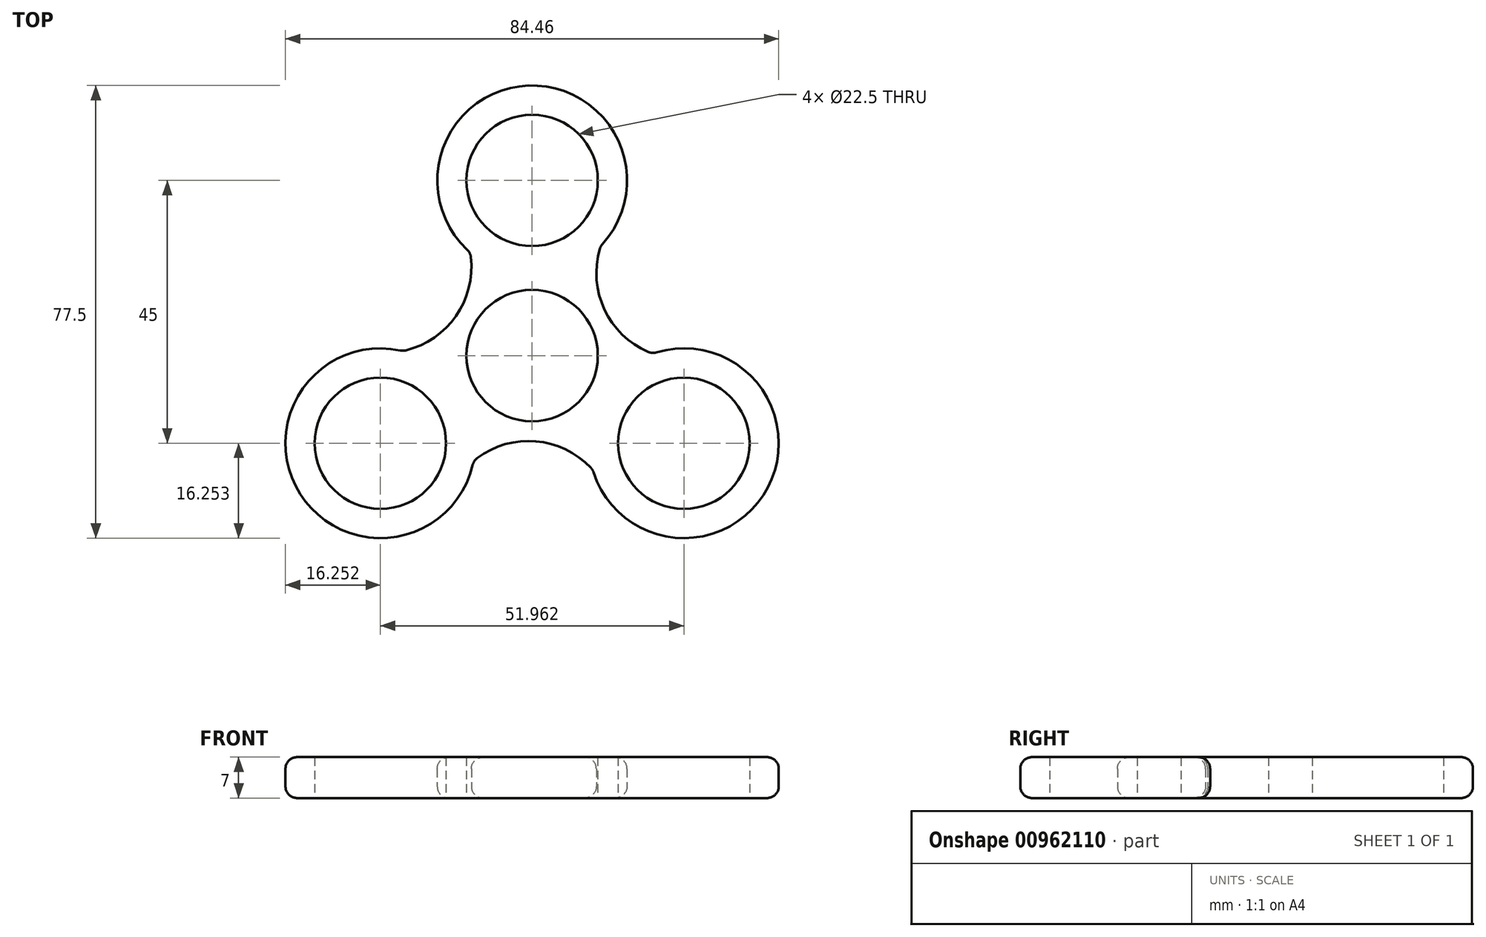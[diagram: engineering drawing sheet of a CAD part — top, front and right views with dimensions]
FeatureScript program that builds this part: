
annotation { "Feature Type Name" : "Feature", "Feature Type Description" : "" }
export const myFeature = defineFeature(function(context is Context, id is Id, definition is map)
    precondition{}
    {
        {
            var Q0;
            Q0=qCreatedBy(makeId("Top.planeOp"),FACE);
            var sketch = newSketch(context, id + "F0", { "sketchPlane" : qUnion([Q0])});
            skCircle(sketch, "E0", {"center": v(-12.85, 13.48) * mm, "radius": 11.25 * mm});
            skCircle(sketch, "E1", {"center": v(-12.85, 43.48) * mm, "radius": 11.25 * mm});
            skCircle(sketch, "E2.1.0", {"center": v(-38.83, -1.52) * mm, "radius": 11.25 * mm});
            skCircle(sketch, "E2.2.0", {"center": v(13.13, -1.52) * mm, "radius": 11.25 * mm});
            skCircle(sketch, "E3.0", {"center": v(-12.85, 43.48) * mm, "radius": 16.25 * mm});
            skCircle(sketch, "E4.0", {"center": v(13.13, -1.52) * mm, "radius": 16.25 * mm});
            skCircle(sketch, "E5.0", {"center": v(-38.83, -1.52) * mm, "radius": 16.25 * mm});
            skArc(sketch, "E6", {"start": v(-34.98, 14.27) * mm, "mid": v(-25.8, 20.39) * mm, "end": v(-23.46, 31.18) * mm});
            skArc(sketch, "E7.1.0", {"start": v(-2.46, -6.08) * mm, "mid": v(-12.35, -1.18) * mm, "end": v(-22.86, -4.55) * mm});
            skArc(sketch, "E7.2.0", {"start": v(-1.1, 32.26) * mm, "mid": v(-0.4, 21.24) * mm, "end": v(7.78, 13.83) * mm});
            skSolve(sketch);
        }
        {
            var Q0;
            Q0=makeQuery(id+"F0.imprint","IMPRINT",FACE,{"disambiguationData":[TD([[makeQuery(id+"F0.imprint","IMPRINT",EDGE,{"derivedFrom":sQuery(id+"F0.wireOp",EDGE,"E1")}),-1.0]])]});
            var Q1;
            Q1=makeQuery(id+"F0.imprint","IMPRINT",FACE,{"disambiguationData":[TD([[makeQuery(id+"F0.imprint","IMPRINT",EDGE,{"derivedFrom":sQuery(id+"F0.wireOp",EDGE,"E0")}),-1.0]])]});
            var Q2;
            Q2=makeQuery(id+"F0.imprint","IMPRINT",FACE,{"disambiguationData":[TD([[makeQuery(id+"F0.imprint","IMPRINT",EDGE,{"derivedFrom":sQuery(id+"F0.wireOp",EDGE,"E2.1.0")}),-1.0]])]});
            var Q3;
            Q3=makeQuery(id+"F0.imprint","IMPRINT",FACE,{"disambiguationData":[TD([[makeQuery(id+"F0.imprint","IMPRINT",EDGE,{"derivedFrom":sQuery(id+"F0.wireOp",EDGE,"E2.2.0")}),-1.0]])]});
            extrude(context, id + "F1", {"entities" : qUnion([Q0, Q1, Q2, Q3]), "depth" : 7 * mm, "offsetDistance" : 25 * mm});
        }
        {
            var Q0;
            Q0=makeQuery(id+"F1.opExtrude","SWEPT_FACE",FACE,{"disambiguationData":[OSD([sQuery(id+"F0.wireOp",EDGE,"E7.2.0")])]});
            var Q1;
            Q1=makeQuery(id+"F1.opExtrude","SWEPT_FACE",FACE,{"disambiguationData":[OSD([sQuery(id+"F0.wireOp",EDGE,"E3.0")])]});
            var Q2;
            Q2=makeQuery(id+"F1.opExtrude","SWEPT_FACE",FACE,{"disambiguationData":[OSD([sQuery(id+"F0.wireOp",EDGE,"E6")])]});
            var Q3;
            Q3=makeQuery(id+"F1.opExtrude","SWEPT_FACE",FACE,{"disambiguationData":[OSD([sQuery(id+"F0.wireOp",EDGE,"E5.0")])]});
            var Q4;
            Q4=makeQuery(id+"F1.opExtrude","SWEPT_FACE",FACE,{"disambiguationData":[OSD([sQuery(id+"F0.wireOp",EDGE,"E7.1.0")])]});
            var Q5;
            Q5=makeQuery(id+"F1.opExtrude","SWEPT_FACE",FACE,{"disambiguationData":[OSD([sQuery(id+"F0.wireOp",EDGE,"E4.0")])]});
            fillet(context, id + "F2", {"entities" : qUnion([Q0, Q1, Q2, Q3, Q4, Q5]), "radius" : 2 * mm, "tangentPropagation" : true, "allowEdgeOverflow" : false});
        }
    });
